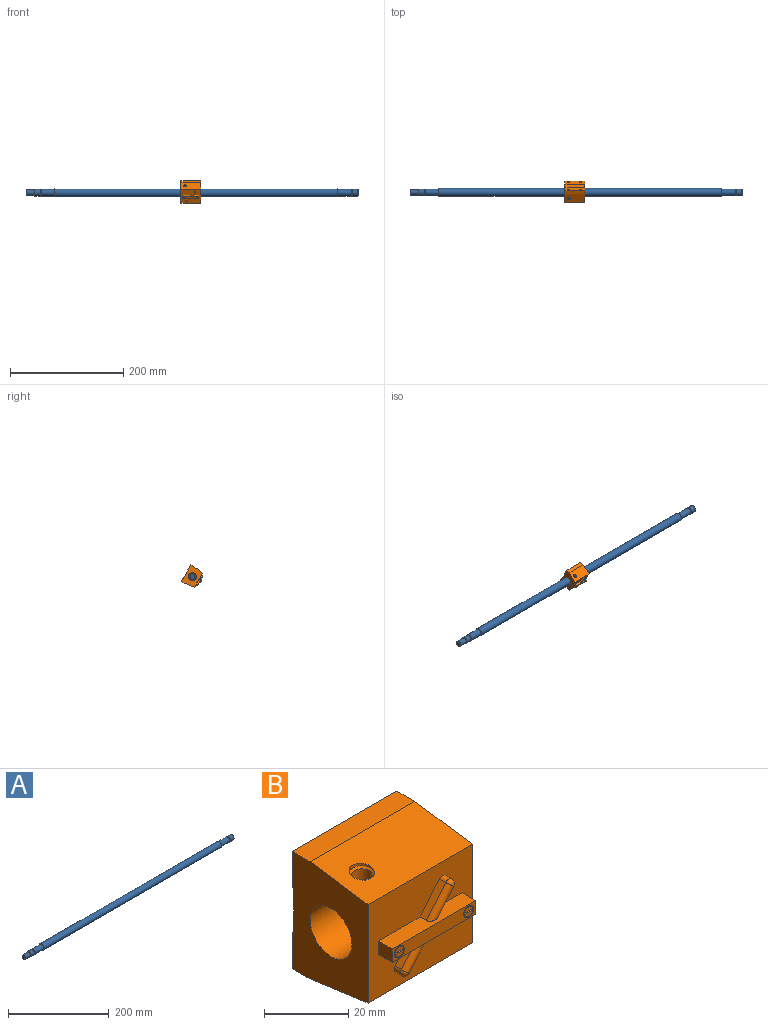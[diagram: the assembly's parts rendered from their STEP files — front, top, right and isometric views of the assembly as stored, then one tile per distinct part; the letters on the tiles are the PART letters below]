
ASSEMBLY  parts=2 mates=1
PART A: 20 faces, bbox 587x14x14 mm
  f0: plane 8.5x8.5mm, normal (-1,0,0), area 56.7mm2, adj f1
  f1: cone r=4.62mm half-angle=45deg, axis (1,0,0), area 30.8mm2, adj f0,f2
  f2: cylinder r=5mm len=14.25mm, axis (1,0,0), area 447.7mm2, adj f1,f3
  f3: plane 10.77x10.77mm, normal (-1,0,0), area 12.6mm2, adj f2,f4
  f4: cone r=5.69mm half-angle=45deg, axis (1,0,0), area 31mm2, adj f3,f5
  f5: cylinder r=6mm len=12mm, axis (1,0,0), area 353.9mm2, adj f4,f6
  f6: plane 12x12mm, normal (1,0,0), area 29.8mm2, adj f5,f7
  f7: cylinder r=5.15mm len=10.3mm, axis (1,0,0), area 64.7mm2, adj f6,f9
  f8: plane 10.77x10.77mm, normal (1,0,0), area 91.2mm2, adj f10
  f9: plane 12x12mm, normal (-1,0,0), area 29.8mm2, adj f7,f11
  f10: cone r=5.69mm half-angle=45deg, axis (-1,0,0), area 31mm2, adj f8,f12
  f11: cylinder r=6mm len=24mm, axis (1,0,0), area 904.8mm2, adj f9,f13
  f12: cylinder r=6mm len=12mm, axis (-1,0,0), area 353.9mm2, adj f10,f14
  f13: plane 14x14mm, normal (-1,0,0), area 40.8mm2, adj f11,f15
  f14: plane 12x12mm, normal (-1,0,0), area 29.8mm2, adj f12,f16
  f15: cylinder r=7mm len=500mm, axis (-1,0,0), area 21991.1mm2, adj f13,f17
  f16: cylinder r=5.15mm len=10.3mm, axis (-1,0,0), area 64.7mm2, adj f14,f18
  f17: plane 14x14mm, normal (1,0,0), area 40.8mm2, adj f15,f19
  f18: plane 12x12mm, normal (1,0,0), area 29.8mm2, adj f16,f19
  f19: cylinder r=6mm len=24mm, axis (-1,0,0), area 904.8mm2, adj f17,f18
PART B: 65 faces, bbox 35x30x34 mm
  f0: plane 2.78x1.2mm, normal (0,-1,0), area 2.5mm2, adj f1,f10
  f1: plane 2.86x0.45mm, normal (0,0,1), area 1.3mm2, adj f0,f2,f10
  f2: plane 2.89x0.4mm, normal (0,-1,0), area 1.2mm2, adj f1,f3,f10
  f3: plane 2.86x0.45mm, normal (0,0,-1), area 1.3mm2, adj f2,f4,f10
  f4: plane 2.78x1.2mm, normal (0,-1,0), area 2.5mm2, adj f3,f10
  f5: plane 2.78x1.2mm, normal (0,-1,0), area 2.5mm2, adj f6,f11
  f6: plane 2.86x0.45mm, normal (0,0,1), area 1.3mm2, adj f5,f7,f11
  f7: plane 2.89x0.4mm, normal (0,-1,0), area 1.2mm2, adj f6,f8,f11
  f8: plane 2.86x0.45mm, normal (0,0,-1), area 1.3mm2, adj f7,f9,f11
  f9: plane 2.78x1.2mm, normal (0,-1,0), area 2.5mm2, adj f8,f11
  f10: cone r=1.45mm half-angle=5deg, axis (0,1,0), area 9.7mm2, adj f0,f1,f2,f3,f4,f15
  f11: cone r=1.45mm half-angle=5deg, axis (0,1,0), area 9.7mm2, adj f5,f6,f7,f8,f9,f16
  f12: plane 6x6mm, normal (0,0,1), area 28.3mm2, adj f17
  f13: plane 4x4mm, normal (0,1,0), area 12.6mm2, adj f20
  f14: plane 4x4mm, normal (0,1,0), area 12.6mm2, adj f21
  f15: plane 3.3x3.3mm, normal (0,-1,0), area 1.5mm2, adj f10,f22
  f16: plane 3.3x3.3mm, normal (0,-1,0), area 1.5mm2, adj f11,f23
  f17: cone r=2.73mm half-angle=45deg, axis (0,0,-1), area 13.1mm2, adj f12,f24
  f18: plane 4x4mm, normal (0,1,0), area 12.6mm2, adj f25
  f19: plane 4x4mm, normal (0,1,0), area 12.6mm2, adj f26
  f20: cone r=1.81mm half-angle=45deg, axis (0,-1,0), area 6.1mm2, adj f13,f27
  f21: cone r=1.81mm half-angle=45deg, axis (0,-1,0), area 6.1mm2, adj f14,f28
  f22: cylinder r=1.65mm len=3.3mm, axis (0,1,0), area 11.4mm2, adj f15,f31
  f23: cylinder r=1.65mm len=3.3mm, axis (0,1,0), area 11.4mm2, adj f16,f31
  f24: cylinder r=2.46mm len=4.92mm, axis (0,0,-1), area 60.5mm2, adj f17,f34
  f25: cone r=1.81mm half-angle=45deg, axis (0,-1,0), area 6.1mm2, adj f18,f35
  f26: cone r=1.81mm half-angle=45deg, axis (0,-1,0), area 6.1mm2, adj f19,f36
  f27: cylinder r=1.62mm len=6.24mm, axis (0,-1,0), area 63.6mm2, adj f20,f37
  f28: cylinder r=1.62mm len=6.24mm, axis (0,-1,0), area 63.6mm2, adj f21,f38
  f29: sphere r=1.31mm, area 5.4mm2, adj f30,f41
  f30: cylinder r=1.31mm len=9.47mm, axis (0.64,0,0.77), area 37.3mm2, adj f29,f40,f42,f43
  f31: plane 28x3.9mm, normal (0,-1,0), area 92.1mm2, adj f22,f23,f39,f43,f44,f45
  f32: sphere r=1.31mm, area 5.4mm2, adj f33,f47
  f33: cylinder r=1.31mm len=9.47mm, axis (0.64,0,0.77), area 37.3mm2, adj f32,f45,f46,f48
  f34: cone r=2.73mm half-angle=45deg, axis (0,0,1), area 13.1mm2, adj f24,f49
  f35: cylinder r=1.62mm len=6.24mm, axis (0,-1,0), area 63.6mm2, adj f25,f50
  f36: cylinder r=1.62mm len=6.24mm, axis (0,-1,0), area 63.6mm2, adj f26,f51
  f37: cone r=1.81mm half-angle=45deg, axis (0,1,0), area 6.1mm2, adj f27,f54
  f38: cone r=1.81mm half-angle=45deg, axis (0,1,0), area 6.1mm2, adj f28,f54
  f39: plane 4.6x3.9mm, normal (-1,0,0), area 17.9mm2, adj f31,f43,f45,f57
  f40: plane 6.1x5.12mm, normal (-0.77,0,0.64), area 16.6mm2, adj f30,f41,f43,f57
  f41: cylinder r=1.31mm len=2.31mm, axis (0,-1,0), area 8.6mm2, adj f29,f40,f42,f57
  f42: plane 7.78x6.53mm, normal (0.77,0,-0.64), area 21.1mm2, adj f30,f41,f43,f57
  f43: plane 28x4.6mm, normal (0,0,-1), area 118.2mm2, adj f30,f31,f39,f40,f42,f44,f57
  f44: plane 4.6x3.9mm, normal (1,0,0), area 17.9mm2, adj f31,f43,f45,f57
  f45: plane 28x4.6mm, normal (0,0,1), area 118.2mm2, adj f31,f33,f39,f44,f46,f48,f57
  f46: plane 6.1x5.12mm, normal (0.77,0,-0.64), area 16.6mm2, adj f33,f45,f47,f57
  f47: cylinder r=1.31mm len=2.31mm, axis (0,-1,0), area 8.6mm2, adj f32,f46,f48,f57
  f48: plane 7.78x6.53mm, normal (-0.77,0,0.64), area 21.1mm2, adj f33,f45,f47,f57
  f49: cylinder r=3mm len=6mm, axis (0,0,-1), area 7.9mm2, adj f34,f58
  f50: cone r=1.81mm half-angle=45deg, axis (0,1,0), area 6.1mm2, adj f35,f60
  f51: cone r=1.81mm half-angle=45deg, axis (0,1,0), area 6.1mm2, adj f36,f60
  f52: plane 35x13mm, normal (0,1,0), area 455mm2, adj f53,f61,f62,f63
  f53: plane 35x0.6mm, normal (0,0,1), area 21mm2, adj f52,f54,f62,f63
  f54: plane 35x10.5mm, normal (0,1,0), area 342.4mm2, adj f37,f38,f53,f55,f62,f63
  f55: plane 35x6mm, normal (0,0,-1), area 210mm2, adj f54,f56,f62,f63
  f56: plane 35x19.4mm, normal (0,-0.14,-0.99), area 685.7mm2, adj f55,f57,f62,f63
  f57: plane 35x28.55mm, normal (0,-1,0), area 837.1mm2, adj f39,f40,f41,f42,f43,f44,f45,f46
  f58: plane 35x19.4mm, normal (0,-0.14,0.99), area 657.1mm2, adj f49,f57,f59,f62,f63
  f59: plane 35x6mm, normal (0,0,1), area 210mm2, adj f58,f60,f62,f63
  f60: plane 35x10.5mm, normal (0,1,0), area 342.4mm2, adj f50,f51,f59,f61,f62,f63
  f61: plane 35x0.6mm, normal (0,0,-1), area 21mm2, adj f52,f60,f62,f63
  f62: plane 34x25.4mm, normal (-1,0,0), area 649mm2, adj f52,f53,f54,f55,f56,f57,f58,f59
  f63: plane 34x25.4mm, normal (1,0,0), area 649mm2, adj f52,f53,f54,f55,f56,f57,f58,f59
  f64: cylinder r=7mm len=35mm, axis (1,0,0), area 1539.4mm2, adj f62,f63
PLACE A t=(106.03,124.81,-43.95)mm fixed
PLACE B rot(axis=(1,0,0),29.9deg) t=(96.45,124.81,-43.95)mm
MATE cylindrical A.f10 <-> B.f64  axis (-1,0,0) through (407.03,124.81,-43.95)mm
